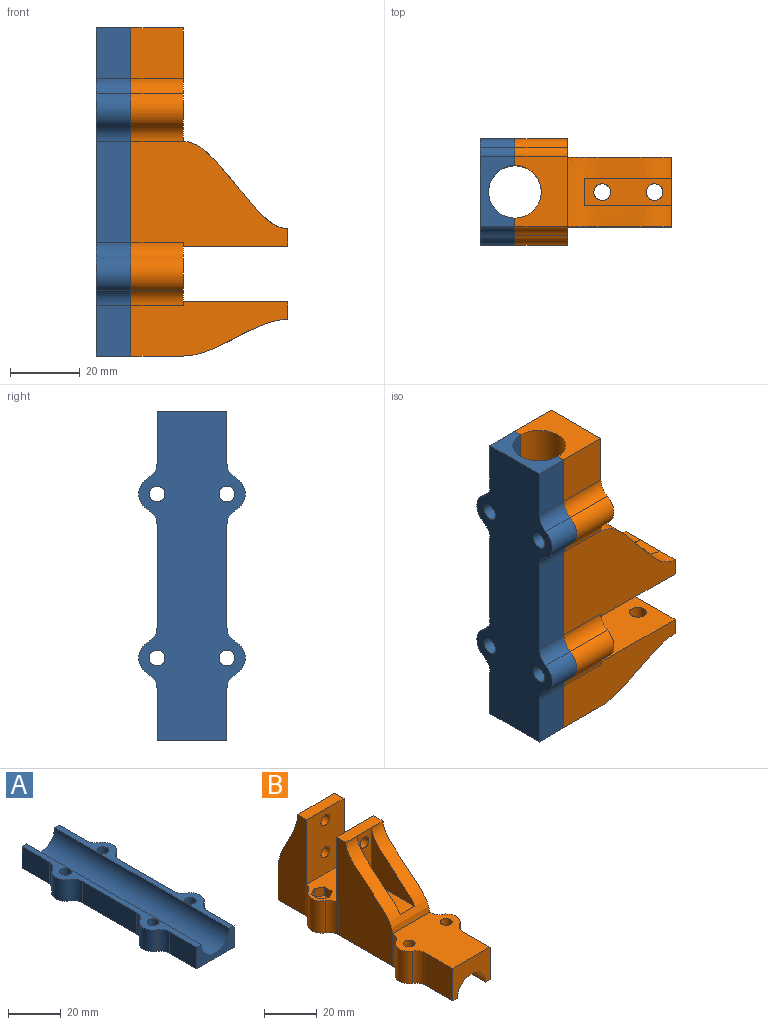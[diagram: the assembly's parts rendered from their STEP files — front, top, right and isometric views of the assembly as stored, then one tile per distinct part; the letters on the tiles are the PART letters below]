
ASSEMBLY  parts=2 mates=1
PART A: 28 faces, bbox 30.5x94x10 mm
  f0: plane 94x7.7mm, normal (0,0,1), area 293.4mm2, adj f2,f3,f4,f5,f6,f16,f17,f18
  f1: cylinder r=2.25mm len=10mm, axis (0,0,1), area 141.4mm2, adj f25,f27
  f2: cylinder r=2.25mm len=10mm, axis (0,0,1), area 141.4mm2, adj f0,f25
  f3: cylinder r=2.25mm len=10mm, axis (0,0,1), area 141.4mm2, adj f0,f25
  f4: cylinder r=7.55mm len=94mm, axis (0,1,0), area 2229.6mm2, adj f0,f6,f16,f27
  f5: plane 14.55x10mm, normal (-1,0,0), area 145.5mm2, adj f0,f6,f24,f25
  f6: plane 20x10mm, normal (0,1,0), area 110.5mm2, adj f0,f4,f5,f7,f25,f27
  f7: plane 14.55x10mm, normal (1,0,0), area 145.5mm2, adj f6,f8,f25,f27
  f8: cylinder r=5mm len=10mm, axis (0,0,1), area 53.1mm2, adj f7,f9,f25,f27
  f9: cylinder r=5.25mm len=10mm, axis (0,0,1), area 111.4mm2, adj f8,f10,f25,f27
  f10: cylinder r=5mm len=10mm, axis (0,0,1), area 53.1mm2, adj f9,f11,f25,f27
  f11: plane 29.1x10mm, normal (1,0,0), area 291mm2, adj f10,f12,f25,f27
  f12: cylinder r=5mm len=10mm, axis (0,0,1), area 53.1mm2, adj f11,f13,f25,f27
  f13: cylinder r=5.25mm len=10mm, axis (0,0,1), area 111.4mm2, adj f12,f14,f25,f27
  f14: cylinder r=5mm len=10mm, axis (0,0,1), area 53.1mm2, adj f13,f15,f25,f27
  f15: plane 14.55x10mm, normal (1,0,0), area 145.5mm2, adj f14,f16,f25,f27
  f16: plane 20x10mm, normal (0,-1,0), area 110.5mm2, adj f0,f4,f15,f17,f25,f27
  f17: plane 14.55x10mm, normal (-1,0,0), area 145.5mm2, adj f0,f16,f18,f25
  f18: cylinder r=5mm len=10mm, axis (0,0,1), area 53.1mm2, adj f0,f17,f19,f25
  f19: cylinder r=5.25mm len=10mm, axis (0,0,1), area 111.4mm2, adj f0,f18,f20,f25
  f20: cylinder r=5mm len=10mm, axis (0,0,1), area 53.1mm2, adj f0,f19,f21,f25
  f21: plane 29.1x10mm, normal (-1,0,0), area 291mm2, adj f0,f20,f22,f25
  f22: cylinder r=5mm len=10mm, axis (0,0,1), area 53.1mm2, adj f0,f21,f23,f25
  f23: cylinder r=5.25mm len=10mm, axis (0,0,1), area 111.4mm2, adj f0,f22,f24,f25
  f24: cylinder r=5mm len=10mm, axis (0,0,1), area 53.1mm2, adj f0,f5,f23,f25
  f25: plane 94x30.5mm, normal (0,0,-1), area 2006.2mm2, adj f1,f2,f3,f5,f6,f7,f8,f9
  f26: cylinder r=2.25mm len=10mm, axis (0,0,1), area 141.4mm2, adj f25,f27
  f27: plane 94x7.7mm, normal (0,0,1), area 293.4mm2, adj f1,f4,f6,f7,f8,f9,f10,f11
PART B: 61 faces, bbox 31.3x94.8x45.8 mm
  f0: plane 30.5x17.9mm, normal (0,0,1), area 327.6mm2, adj f4,f5,f6,f7,f17,f18,f19,f20
  f1: cylinder r=2.25mm len=11mm, axis (0,0,1), area 155.5mm2, adj f27,f54
  f2: cylinder r=2.25mm len=11mm, axis (0,0,1), area 155.5mm2, adj f28,f53
  f3: bspline ~30x25mm, area 532.4mm2, adj f7,f17,f29,f33,f36,f37,f38
  f4: cylinder r=5mm len=15mm, axis (0,0,1), area 79.6mm2, adj f0,f5,f25,f27
  f5: cylinder r=5.25mm len=15mm, axis (0,0,1), area 167.1mm2, adj f0,f4,f6,f27
  f6: cylinder r=5mm len=15mm, axis (0,0,1), area 79.6mm2, adj f0,f5,f7,f27
  f7: plane 45x30.05mm, normal (-1,0,0), area 961.6mm2, adj f0,f3,f6,f8,f27,f29,f33,f34
  f8: cylinder r=5mm len=15mm, axis (0,0,1), area 79.6mm2, adj f7,f9,f27,f29
  f9: cylinder r=5.25mm len=15mm, axis (0,0,1), area 167.1mm2, adj f8,f10,f27,f29
  f10: cylinder r=5mm len=15mm, axis (0,0,1), area 79.6mm2, adj f9,f11,f27,f29
  f11: plane 15x14.55mm, normal (-1,0,0), area 218.3mm2, adj f10,f12,f27,f29
  f12: plane 20x15mm, normal (0,-1,0), area 210.5mm2, adj f11,f13,f26,f27,f28,f29
  f13: plane 15x14.55mm, normal (1,0,0), area 218.3mm2, adj f12,f14,f28,f29
  f14: cylinder r=5mm len=15mm, axis (0,0,1), area 79.6mm2, adj f13,f15,f28,f29
  f15: cylinder r=5.25mm len=15mm, axis (0,0,1), area 167.1mm2, adj f14,f16,f28,f29
  f16: cylinder r=5mm len=15mm, axis (0,0,1), area 79.6mm2, adj f15,f17,f28,f29
  f17: plane 45x30.05mm, normal (1,0,0), area 961.6mm2, adj f0,f3,f16,f18,f28,f29,f33,f34
  f18: cylinder r=5mm len=15mm, axis (0,0,1), area 79.6mm2, adj f0,f17,f19,f28
  f19: cylinder r=5.25mm len=15mm, axis (0,0,1), area 167.1mm2, adj f0,f18,f20,f28
  f20: cylinder r=5mm len=15mm, axis (0,0,1), area 79.6mm2, adj f0,f19,f21,f28
  f21: plane 45x15.5mm, normal (1,0,0), area 525.8mm2, adj f0,f20,f22,f28,f30,f31,f32
  f22: plane 20x15mm, normal (0,1,0), area 210.5mm2, adj f21,f25,f26,f27,f28,f32
  f23: cylinder r=2.25mm len=15mm, axis (0,0,1), area 212.1mm2, adj f28,f29
  f24: cylinder r=2.25mm len=15mm, axis (0,0,1), area 212.1mm2, adj f27,f29
  f25: plane 45x15.5mm, normal (-1,0,0), area 525.8mm2, adj f0,f4,f22,f27,f30,f31,f32
  f26: cylinder r=7.55mm len=94mm, axis (0,1,0), area 2229.6mm2, adj f12,f22,f27,f28
  f27: plane 94x7.7mm, normal (0,0,-1), area 293.4mm2, adj f1,f4,f5,f6,f7,f8,f9,f10
  f28: plane 94x7.7mm, normal (0,0,-1), area 293.4mm2, adj f2,f12,f13,f14,f15,f16,f17,f18
  f29: plane 32.5x30.5mm, normal (0,0,1), area 713.1mm2, adj f3,f7,f8,f9,f10,f11,f12,f13
  f30: plane 20x5mm, normal (0,0,1), area 100mm2, adj f21,f25,f31,f32,f40
  f31: plane 30x20mm, normal (0,-1,0), area 563.8mm2, adj f0,f21,f25,f30,f43,f44
  f32: bspline ~30x20mm, area 431.3mm2, adj f21,f22,f25,f30,f39,f41,f42
  f33: plane 20x5mm, normal (0,0,1), area 100mm2, adj f3,f7,f17,f34,f35
  f34: plane 30x20mm, normal (0,1,0), area 563.8mm2, adj f0,f7,f17,f33,f45,f46
  f35: plane 25x7.8mm, normal (0,-1,0), area 158.8mm2, adj f33,f36,f37,f38,f45,f46
  f36: plane 25x23.21mm, normal (1,0,0), area 253.1mm2, adj f3,f35,f38
  f37: plane 25x23.21mm, normal (-1,0,0), area 253.1mm2, adj f3,f35,f38
  f38: plane 23.21x7.8mm, normal (0,0,1), area 181mm2, adj f3,f35,f36,f37
  f39: plane 25.76x10.49mm, normal (1,0,0), area 106.3mm2, adj f32,f40,f42
  f40: plane 25x7.8mm, normal (0,1,0), area 158.8mm2, adj f30,f39,f41,f42,f43,f44
  f41: plane 25.76x10.49mm, normal (-1,0,0), area 106.3mm2, adj f32,f40,f42
  f42: plane 9.73x7.8mm, normal (0,0,1), area 75.9mm2, adj f32,f39,f40,f41
  f43: cylinder r=2.4mm len=5mm, axis (0,1,0), area 75.4mm2, adj f31,f40
  f44: cylinder r=2.4mm len=5mm, axis (0,1,0), area 75.4mm2, adj f31,f40
  f45: cylinder r=2.4mm len=5mm, axis (0,1,0), area 75.4mm2, adj f34,f35
  f46: cylinder r=2.4mm len=5mm, axis (0,1,0), area 75.4mm2, adj f34,f35
  f47: plane 4x3.55mm, normal (-0.5,0.87,0), area 16.4mm2, adj f0,f48,f52,f53
  f48: plane 4.1x4mm, normal (-1,0,0), area 16.4mm2, adj f0,f47,f49,f53
  f49: plane 4x3.55mm, normal (-0.5,-0.87,0), area 16.4mm2, adj f0,f48,f50,f53
  f50: plane 4x3.55mm, normal (0.5,-0.87,0), area 16.4mm2, adj f0,f49,f51,f53
  f51: plane 4.1x4mm, normal (1,0,0), area 16.4mm2, adj f0,f50,f52,f53
  f52: plane 4x3.55mm, normal (0.5,0.87,0), area 16.4mm2, adj f0,f47,f51,f53
  f53: plane 8.2x7.1mm, normal (0,0,1), area 27.8mm2, adj f2,f47,f48,f49,f50,f51,f52
  f54: plane 8.2x7.1mm, normal (0,0,1), area 27.8mm2, adj f1,f55,f56,f57,f58,f59,f60
  f55: plane 4.1x4mm, normal (1,0,0), area 16.4mm2, adj f0,f54,f56,f60
  f56: plane 4x3.55mm, normal (0.5,0.87,0), area 16.4mm2, adj f0,f54,f55,f57
  f57: plane 4x3.55mm, normal (-0.5,0.87,0), area 16.4mm2, adj f0,f54,f56,f58
  f58: plane 4.1x4mm, normal (-1,0,0), area 16.4mm2, adj f0,f54,f57,f59
  f59: plane 4x3.55mm, normal (-0.5,-0.87,0), area 16.4mm2, adj f0,f54,f58,f60
  f60: plane 4x3.55mm, normal (0.5,-0.87,0), area 16.4mm2, adj f0,f54,f55,f59
PLACE A rot(axis=(-0.58,0.58,-0.58),120deg) t=(-78.95,0,5)mm
PLACE B rot(axis=(-0.58,0.58,-0.58),120deg) t=(-78.95,0,5)mm
MATE fastened B.f2 <-> A.f26  axis (-1,0,0) through (-78.95,-10,5)mm
